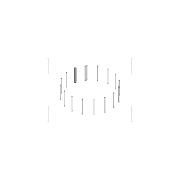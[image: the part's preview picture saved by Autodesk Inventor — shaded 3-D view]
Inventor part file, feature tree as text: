
AUTODESK INVENTOR PART (.ipt)
format: ipt  version: 2021 (Build 250183000, 183)  size: 144,896 bytes
history: native  units: in
note: dims shown in document units (in); Inventor stores cm internally (conversion verified against a paired STEP export)
features: extrude x1, sketch x1
ambient origin geometry x8: Origin, YZ Plane, XZ Plane, XY Plane, X Axis, Y Axis, Z Axis, Center Point
bodies: Solid1 (feature_tree)
feature tree (2):
  extrude  "Extrusion1"  Depth=393.7008in TaperAngle=360.0deg
  sketch  "Sketch1"  dims[d0=393.7008in d1=6.2992in d3=360.0deg d5=118.1102in d6=0.0in d7=393.7008in d8=1.5748in d10=360.0deg]
